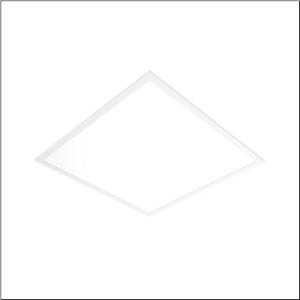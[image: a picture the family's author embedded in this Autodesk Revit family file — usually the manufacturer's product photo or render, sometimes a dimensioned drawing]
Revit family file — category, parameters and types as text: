
# Revit family: apollon_r__41_51mh12wd2422_e36b
name_source: partatom
category: Lighting Fixtures
units: mm (PartAtom-declared; Revit-internal decimal feet)

## family parameters
Cut with Voids When Loaded = No
Host = Face
Light Source = No
Part Type = Normal
Room Calculation Point = No
Round Connector Dimension = Use Diameter
Shared = No

## types (1)
- Apollon® 41 (1 x LED, 3700 lm, 35 W, 4000K)
    Apparent Load = 35 VA
    CIE Flux Codes = 63 87 97 100 100
    Color Rendering = 80
    Color Temperature = 4000K
    Default Elevation = 1800 mm
    Description = Apollon® 41, office luminaire, primary optical cover: prismatic diffuser, of PS, light emission: direct distribution, primary light characteristic: symmetric, installation type: lay-in mounting, LED, rated luminous flux: 3.700lm, luminous efficacy: 105lm/W, light colour: 840, colour temperature: 4000K, control gear: ECG DALI, with terminal, 5-pole, mains connection: 220..240V, AC, 50/60Hz, rated input power: 35W, housing, of aluminium section, traffic white (RAL 9016), module: M600, length: 595mm, width: 595mm, height: 32mm, housing upper side, of sheet steel, protection rating (complete): IP20, protection rating (lamp compartment, on room side): IP40, insulation class (complete): insulation class II (safety insulation), certification: CE, ENEC, permissible operating ambient temperature: -20..+40°C, packaging unit: 1 piece
    Height = 0 mm  [stored 0 ft]
    Lamp = 1 x LED
    Lamp Light Flux = 3700 lm
    Lamp Power = 35 W
    Lamp count = 1
    Length = 596 mm
    Luminous efficacy = 106 lm/W
    Manufacturer = Siteco
    ModVariant = No
    Model = 51MH12WD2422
    Mounting Place = Ceiling
    Mounting Type = Recessed
    Number of Poles = 1
    OnlyDefault = Yes
    Power Factor = 1
    Product Name = Apollon® 41
    Product group = office luminaire | ceiling recessed
    ProductGroupID = 401
    Protection Class = Protection class II
    Protection Degree = IP 20
    RLX_Detail_Level = 1
    RLX_Emergency_Light_Flux = 0 lm
    RLX_Emergency_Type = 0
    RLX_Emergency_Type_DB = No
    RlxData = <blob elided: 14857 chars, md5=6f0e61cc>
    Socket = socket
    Standby Power = 0 W
    System Light Flux = 3700 lm
    System Power = 35 W
    Type Comments = Product without accessories
    Type Image = l_1291024.jpg
    URL = http://relux.com
    VarID = ---
    Voltage = 0 V
    Weight = 0.00 kg
    Width = 596 mm

note: [stored X ft] marks values corroborated as IEEE doubles in the binary element streams (Revit-internal decimal feet)

## geometry (parser evidence)
native form markers: Sweep x12
no freeform markers — native parametric forms only
